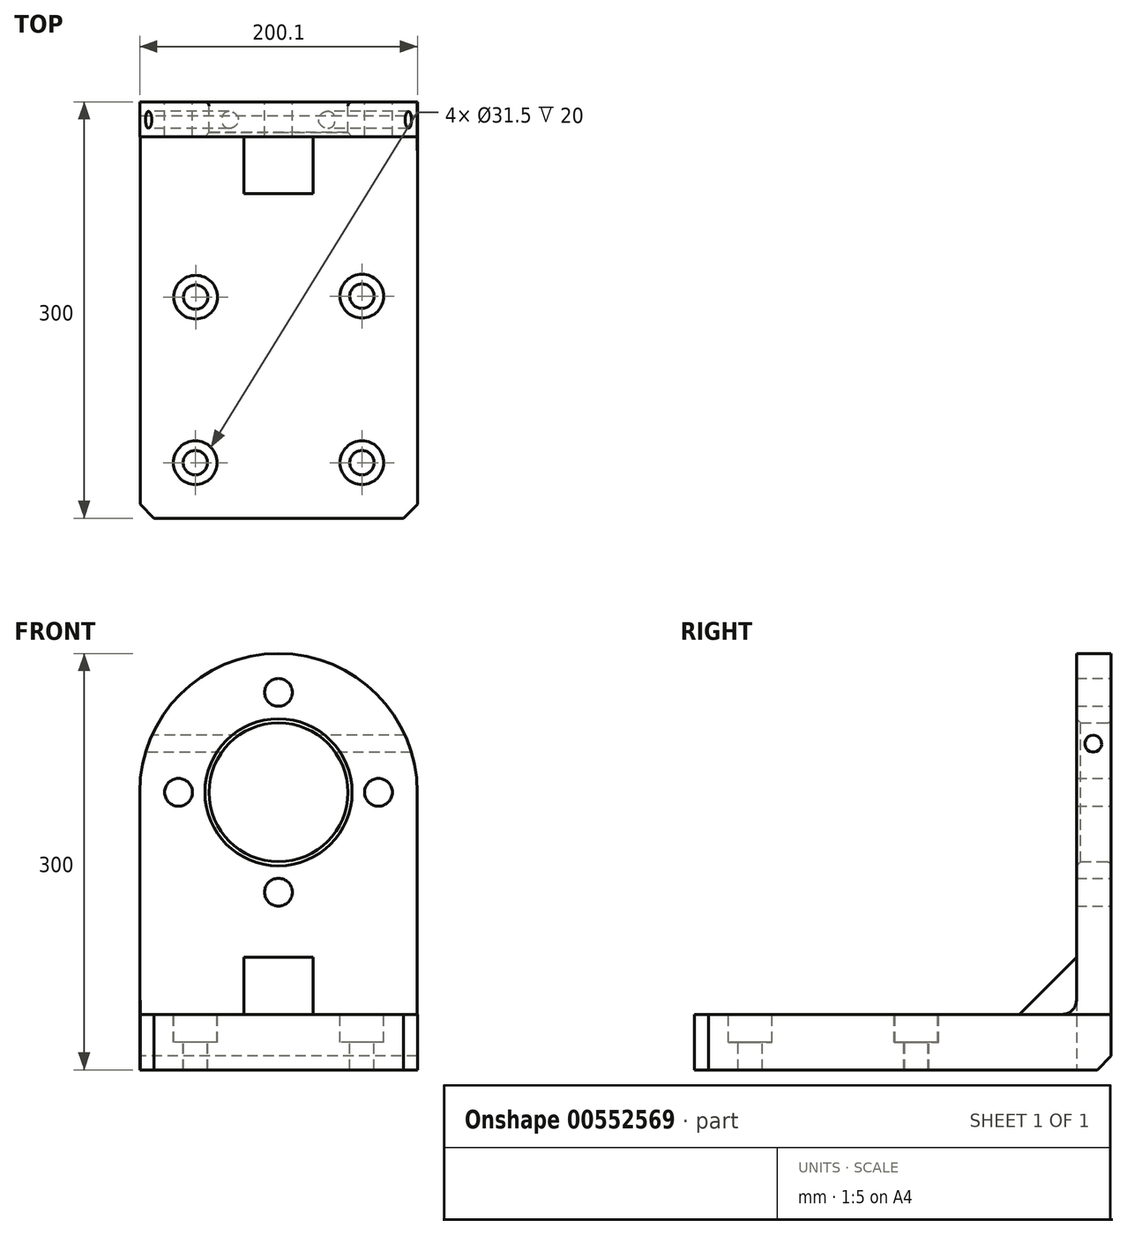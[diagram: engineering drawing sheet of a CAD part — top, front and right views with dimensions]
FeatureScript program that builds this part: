
annotation { "Feature Type Name" : "Feature", "Feature Type Description" : "" }
export const myFeature = defineFeature(function(context is Context, id is Id, definition is map)
    precondition{}
    {
        {
            var Q0;
            Q0=qCreatedBy(makeId("Front.planeOp"),FACE);
            var sketch = newSketch(context, id + "F0", { "sketchPlane" : qUnion([Q0])});
            skLineSegment(sketch, "E0.bottom", {"start": v(-100, 0) * mm, "end": v(100, 0) * mm});
            skLineSegment(sketch, "E0.top", {"start": v(-100, 200) * mm, "end": v(100, 200) * mm});
            skLineSegment(sketch, "E0.left", {"start": v(-100, 0) * mm, "end": v(-100, 200) * mm});
            skLineSegment(sketch, "E0.right", {"start": v(100, 0) * mm, "end": v(100, 200) * mm});
            skArc(sketch, "E1", {"start": v(100, 200) * mm, "mid": v(0, 300) * mm, "end": v(-100, 200) * mm});
            skCircle(sketch, "E2", {"center": v(0, 200) * mm, "radius": 50 * mm});
            skCircle(sketch, "E3", {"center": v(0, 272) * mm, "radius": 10 * mm});
            skCircle(sketch, "E4", {"center": v(0, 200) * mm, "radius": 72 * mm, "construction": true});
            skCircle(sketch, "E5", {"center": v(72, 200) * mm, "radius": 10 * mm});
            skCircle(sketch, "E6", {"center": v(-72, 200) * mm, "radius": 10 * mm});
            skCircle(sketch, "E7", {"center": v(0, 128) * mm, "radius": 10 * mm});
            skLineSegment(sketch, "E8", {"start": v(-100, 200) * mm, "end": v(100, 200) * mm, "construction": true});
            skLineSegment(sketch, "E9", {"start": v(0, 0) * mm, "end": v(0, 300) * mm, "construction": true});
            skSolve(sketch);
        }
        {
            var Q0;
            Q0 = qSketchRegion(id + "F0", true);
            var Q1;
            {var subQ0=sQuery(id+"F0.wireOp",EDGE,"E5");var subQ1=sQuery(id+"F0.wireOp",EDGE,"E0.top");var subQ2=makeQuery(id+"F0.imprint","INTERSECT",VERTEX,{"disambiguationData":[OD(0.0)],"derivedFrom":[subQ1,subQ0]});Q1=makeQuery(id+"F0.imprint","IMPRINT",FACE,{"disambiguationData":[TD([[makeQuery(id+"F0.imprint","IMPRINT",EDGE,{"disambiguationData":[TD([[subQ2,-1.0]])],"derivedFrom":subQ1}),-1.0]])]});}
            var Q2;
            {var subQ0=sQuery(id+"F0.wireOp",EDGE,"E5");var subQ1=sQuery(id+"F0.wireOp",EDGE,"E0.top");var subQ2=makeQuery(id+"F0.imprint","INTERSECT",VERTEX,{"disambiguationData":[OD(0.0)],"derivedFrom":[subQ1,subQ0]});Q2=makeQuery(id+"F0.imprint","IMPRINT",FACE,{"disambiguationData":[TD([[makeQuery(id+"F0.imprint","IMPRINT",EDGE,{"disambiguationData":[TD([[subQ2,-1.0]])],"derivedFrom":subQ1}),1.0]])]});}
            var Q3;
            {var subQ0=sQuery(id+"F0.wireOp",EDGE,"E6");var subQ1=sQuery(id+"F0.wireOp",EDGE,"E0.top");var subQ2=makeQuery(id+"F0.imprint","INTERSECT",VERTEX,{"disambiguationData":[OD(0.0)],"derivedFrom":[subQ1,subQ0]});Q3=makeQuery(id+"F0.imprint","IMPRINT",FACE,{"disambiguationData":[TD([[makeQuery(id+"F0.imprint","IMPRINT",EDGE,{"disambiguationData":[TD([[subQ2,-1.0]])],"derivedFrom":subQ1}),1.0]])]});}
            var Q4;
            {var subQ0=sQuery(id+"F0.wireOp",EDGE,"E6");var subQ1=sQuery(id+"F0.wireOp",EDGE,"E0.top");var subQ2=makeQuery(id+"F0.imprint","INTERSECT",VERTEX,{"disambiguationData":[OD(0.0)],"derivedFrom":[subQ1,subQ0]});Q4=makeQuery(id+"F0.imprint","IMPRINT",FACE,{"disambiguationData":[TD([[makeQuery(id+"F0.imprint","IMPRINT",EDGE,{"disambiguationData":[TD([[subQ2,-1.0]])],"derivedFrom":subQ1}),-1.0]])]});}
            var Q5;
            Q5=makeQuery(id+"F0.imprint","IMPRINT",FACE,{"disambiguationData":[TD([[makeQuery(id+"F0.imprint","IMPRINT",EDGE,{"derivedFrom":sQuery(id+"F0.wireOp",EDGE,"E3")}),1.0]])]});
            var Q6;
            Q6=makeQuery(id+"F0.imprint","IMPRINT",FACE,{"disambiguationData":[TD([[makeQuery(id+"F0.imprint","IMPRINT",EDGE,{"derivedFrom":sQuery(id+"F0.wireOp",EDGE,"E7")}),1.0]])]});
            extrude(context, id + "F1", {"entities" : qUnion([Q0, Q1, Q2, Q3, Q4, Q5, Q6]), "depth" : 25 * mm, "offsetDistance" : 25 * mm});
        }
        {
            var Q0;
            Q0=sQuery(id+"F0.wireOp",VERTEX,"E3.center");
            var Q1;
            Q1=sQuery(id+"F0.wireOp",VERTEX,"E5.center");
            var Q2;
            Q2=sQuery(id+"F0.wireOp",VERTEX,"E7.center");
            var Q3;
            Q3=sQuery(id+"F0.wireOp",VERTEX,"E6.center");
            var Q4;
            Q4=makeQuery(id+"F1.opExtrude","SWEPT_BODY",BODY,{"disambiguationData":[OSD([sQuery(id+"F0.wireOp",EDGE,"E0.bottom"),sQuery(id+"F0.wireOp",EDGE,"E0.left"),sQuery(id+"F0.wireOp",EDGE,"E0.right"),sQuery(id+"F0.wireOp",EDGE,"E1"),sQuery(id+"F0.wireOp",EDGE,"E2")])]});
            hole(context, id + "F2", {"style" : HoleStyle.SIMPLE, "endStyle" : HoleEndStyle.THROUGH, "oppositeDirection" : true, "holeDiameter" : 20 * mm, "isTappedThrough" : true, "tappedDepth" : 12 * mm, "tapClearance" : 3, "locations" : qUnion([Q0, Q1, Q2, Q3]), "scope" : qUnion([Q4])});
        }
        {
            var Q0;
            Q0=qCreatedBy(makeId("Front.planeOp"),FACE);
            var sketch = newSketch(context, id + "F3", { "sketchPlane" : qUnion([Q0])});
            skLineSegment(sketch, "E10.bottom", {"start": v(100.1, 0) * mm, "end": v(-99.6, 0) * mm});
            skLineSegment(sketch, "E10.top", {"start": v(100.1, 40) * mm, "end": v(-99.6, 40) * mm});
            skLineSegment(sketch, "E10.left", {"start": v(100.1, 0) * mm, "end": v(100.1, 40) * mm});
            skLineSegment(sketch, "E10.right", {"start": v(-99.6, 0) * mm, "end": v(-99.6, 40) * mm});
            skSolve(sketch);
        }
        {
            var Q0;
            Q0 = qSketchRegion(id + "F3", true);
            extrude(context, id + "F4", {"entities" : qUnion([Q0]), "operationType" : NewBodyOperationType.ADD, "depth" : 300 * mm, "offsetDistance" : 25 * mm});
        }
        {
            var Q0;
            Q0=qCreatedBy(makeId("Right.planeOp"),FACE);
            var sketch = newSketch(context, id + "F5", { "sketchPlane" : qUnion([Q0])});
            skLineSegment(sketch, "E11.0", {"start": v(-25, 40) * mm, "end": v(-25, 200) * mm});
            skLineSegment(sketch, "E12.0", {"start": v(-300, 40) * mm, "end": v(0, 40) * mm});
            skLineSegment(sketch, "E13", {"start": v(-25, 81.15) * mm, "end": v(-66.15, 40) * mm});
            skSolve(sketch);
        }
        {
            var Q0;
            {var subQ3=sQuery(id+"F5.wireOp",EDGE,"E13");Q0=makeQuery(id+"F5.imprint","IMPRINT",FACE,{"disambiguationData":[TD([[makeQuery(id+"F5.imprint","IMPRINT",EDGE,{"derivedFrom":subQ3}),1.0]])]});}
            extrude(context, id + "F6", {"entities" : qUnion([Q0]), "operationType" : NewBodyOperationType.ADD, "endBound" : BoundingType.SYMMETRIC, "depth" : 50 * mm, "offsetDistance" : 25 * mm});
        }
        {
            var Q0;
            Q0=makeQuery(id+"F4.opExtrude","SWEPT_FACE",FACE,{"disambiguationData":[OSD([sQuery(id+"F3.wireOp",EDGE,"E10.top")])]});
            var sketch = newSketch(context, id + "F7", { "sketchPlane" : qUnion([Q0])});
            skCircle(sketch, "E14", {"center": v(-59.65, -140.7) * mm, "radius": 15.75 * mm});
            skCircle(sketch, "E15", {"center": v(60.1, -140) * mm, "radius": 15.75 * mm});
            skCircle(sketch, "E16", {"center": v(-59.9, -260) * mm, "radius": 15.75 * mm});
            skCircle(sketch, "E17", {"center": v(60.1, -260) * mm, "radius": 15.75 * mm});
            skCircle(sketch, "E18", {"center": v(-59.65, -140.7) * mm, "radius": 10 * mm});
            skSolve(sketch);
        }
        {
            var Q0;
            Q0=sQuery(id+"F7.wireOp",VERTEX,"E14.center");
            var Q1;
            Q1=sQuery(id+"F7.wireOp",VERTEX,"E15.center");
            var Q2;
            Q2=sQuery(id+"F7.wireOp",VERTEX,"E17.center");
            var Q3;
            Q3=sQuery(id+"F7.wireOp",VERTEX,"E16.center");
            var Q4;
            Q4=makeQuery(id+"F1.opExtrude","SWEPT_BODY",BODY,{"disambiguationData":[OSD([sQuery(id+"F0.wireOp",EDGE,"E0.bottom"),sQuery(id+"F0.wireOp",EDGE,"E0.left"),sQuery(id+"F0.wireOp",EDGE,"E0.right"),sQuery(id+"F0.wireOp",EDGE,"E1"),sQuery(id+"F0.wireOp",EDGE,"E2")])]});
            hole(context, id + "F8", {"style" : HoleStyle.C_BORE, "endStyle" : HoleEndStyle.THROUGH, "holeDiameter" : 17.5 * mm, "cBoreDiameter" : 31.5 * mm, "cBoreDepth" : 20 * mm, "isTappedThrough" : true, "tappedDepth" : 12 * mm, "tapClearance" : 3, "locations" : qUnion([Q0, Q1, Q2, Q3]), "scope" : qUnion([Q4])});
        }
        {
            var Q0;
            Q0=makeQuery(id+"F4.opExtrude","CAP_EDGE",EDGE,{"disambiguationData":[OSD([sQuery(id+"F3.wireOp",EDGE,"E10.right")])],"isStart":false});
            var Q1;
            Q1=makeQuery(id+"F4.opExtrude","CAP_EDGE",EDGE,{"disambiguationData":[OSD([sQuery(id+"F3.wireOp",EDGE,"E10.left")])],"isStart":false});
            chamfer(context, id + "F9", {"entities" : qUnion([Q0, Q1]), "width" : 10 * mm, "tangentPropagation" : true});
        }
        {
            var Q0;
            Q0=makeQuery(id+"F1.opExtrude","CAP_EDGE",EDGE,{"disambiguationData":[OSD([sQuery(id+"F0.wireOp",EDGE,"E2")])],"isStart":false});
            chamfer(context, id + "F10", {"entities" : qUnion([Q0]), "width" : 3 * mm, "tangentPropagation" : true});
        }
        {
            var Q0;
            Q0=makeQuery(id+"F1.opExtrude","CAP_EDGE",EDGE,{"disambiguationData":[OSD([sQuery(id+"F0.wireOp",EDGE,"E2")])],"isStart":true});
            fillet(context, id + "F11", {"entities" : qUnion([Q0]), "radius" : 3 * mm, "tangentPropagation" : true, "allowEdgeOverflow" : false});
        }
        {
            var Q0;
            {var subQ0=makeQuery(id+"F1.opExtrude","CAP_FACE",FACE,{"disambiguationData":[OSD([sQuery(id+"F0.wireOp",EDGE,"E0.bottom"),sQuery(id+"F0.wireOp",EDGE,"E0.left"),sQuery(id+"F0.wireOp",EDGE,"E0.right"),sQuery(id+"F0.wireOp",EDGE,"E1"),sQuery(id+"F0.wireOp",EDGE,"E2")])],"isStart":false});var subQ1=makeQuery(id+"F4.opExtrude","SWEPT_FACE",FACE,{"disambiguationData":[OSD([sQuery(id+"F3.wireOp",EDGE,"E10.top")])]});Q0=makeQuery(id+"F6.boolean.opBoolean","SPLIT",EDGE,{"disambiguationData":[TD([makeQuery(id+"F4.opExtrude","SWEPT_FACE",FACE,{"disambiguationData":[OSD([sQuery(id+"F3.wireOp",EDGE,"E10.right")])]})])],"derivedFrom":makeQuery(id+"F4.boolean.opBoolean","INTERSECT",EDGE,{"derivedFrom":[subQ0,subQ1]})});}
            var Q1;
            {var subQ0=sQuery(id+"F0.wireOp",EDGE,"E0.right");var subQ1=makeQuery(id+"F1.opExtrude","CAP_FACE",FACE,{"disambiguationData":[OSD([sQuery(id+"F0.wireOp",EDGE,"E0.bottom"),sQuery(id+"F0.wireOp",EDGE,"E0.left"),subQ0,sQuery(id+"F0.wireOp",EDGE,"E1"),sQuery(id+"F0.wireOp",EDGE,"E2")])],"isStart":false});var subQ2=makeQuery(id+"F4.opExtrude","SWEPT_FACE",FACE,{"disambiguationData":[OSD([sQuery(id+"F3.wireOp",EDGE,"E10.top")])]});Q1=makeQuery(id+"F6.boolean.opBoolean","SPLIT",EDGE,{"disambiguationData":[TD([makeQuery(id+"F1.opExtrude","SWEPT_FACE",FACE,{"disambiguationData":[OSD([subQ0])]})])],"derivedFrom":makeQuery(id+"F4.boolean.opBoolean","INTERSECT",EDGE,{"derivedFrom":[subQ1,subQ2]})});}
            fillet(context, id + "F12", {"entities" : qUnion([Q0, Q1]), "radius" : 10 * mm, "tangentPropagation" : true, "allowEdgeOverflow" : false});
        }
        {
            var Q0;
            Q0=makeQuery(id+"F1.opExtrude","SWEPT_FACE",FACE,{"disambiguationData":[OSD([sQuery(id+"F0.wireOp",EDGE,"E0.left")])]});
            var sketch = newSketch(context, id + "F13", { "sketchPlane" : qUnion([Q0])});
            skPoint(sketch, "E19", {"position": v(12.92, 234.97) * mm});
            skSolve(sketch);
        }
        {
            var Q0;
            Q0=sQuery(id+"F13.wireOp",VERTEX,"E19");
            var Q1;
            Q1=makeQuery(id+"F1.opExtrude","SWEPT_BODY",BODY,{"disambiguationData":[OSD([sQuery(id+"F0.wireOp",EDGE,"E0.bottom"),sQuery(id+"F0.wireOp",EDGE,"E0.left"),sQuery(id+"F0.wireOp",EDGE,"E0.right"),sQuery(id+"F0.wireOp",EDGE,"E1"),sQuery(id+"F0.wireOp",EDGE,"E2")])]});
            hole(context, id + "F14", {"style" : HoleStyle.SIMPLE, "endStyle" : HoleEndStyle.THROUGH, "standardTappedOrClearance" : lookupTablePath({ "standard" : "ISO", "engagement" : "75%", "pitch" : "2 mm", "size" : "M14", "type" : "Tapped" }), "standardBlindInLast" : lookupTablePath({ "standard" : "ISO", "engagement" : "75%", "pitch" : "2 mm", "size" : "M14", "type" : "Tapped" }), "holeDiameter" : 12.1 * mm, "showTappedDepth" : true, "isTappedThrough" : true, "tappedDepth" : 12 * mm, "tapClearance" : 3, "locations" : qUnion([Q0]), "scope" : qUnion([Q1]), "majorDiameter" : 14 * mm});
        }
        {
            var Q0;
            Q0=makeQuery(id+"F4.boolean.opBoolean","MERGE",EDGE,{"derivedFrom":[makeQuery(id+"F1.opExtrude","CAP_EDGE",EDGE,{"disambiguationData":[OSD([sQuery(id+"F0.wireOp",EDGE,"E0.bottom")])],"isStart":true}),makeQuery(id+"F4.opExtrude","CAP_EDGE",EDGE,{"disambiguationData":[OSD([sQuery(id+"F3.wireOp",EDGE,"E10.bottom")])],"isStart":true})]});
            chamfer(context, id + "F15", {"entities" : qUnion([Q0]), "width" : 10 * mm, "tangentPropagation" : true});
        }
    });
